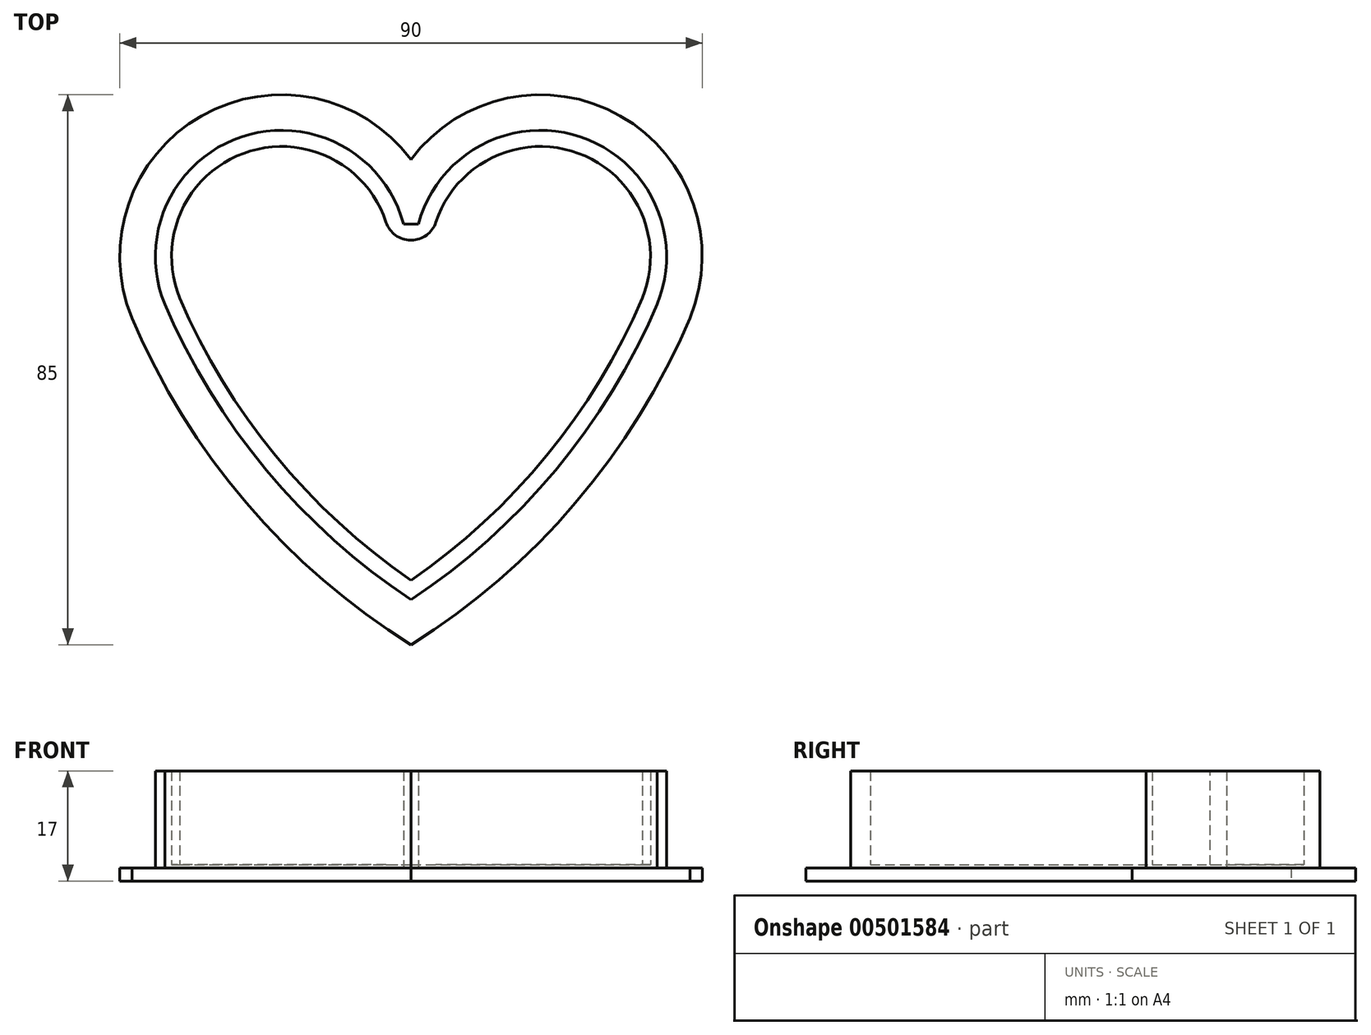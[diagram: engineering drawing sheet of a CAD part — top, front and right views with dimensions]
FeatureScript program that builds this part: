
annotation { "Feature Type Name" : "Feature", "Feature Type Description" : "" }
export const myFeature = defineFeature(function(context is Context, id is Id, definition is map)
    precondition{}
    {
        {
            var Q0;
            Q0=qCreatedBy(makeId("Top.planeOp"),FACE);
            var sketch = newSketch(context, id + "F0", { "sketchPlane" : qUnion([Q0])});
            skArc(sketch, "E0", {"start": v(-43.12, 5.48) * mm, "mid": v(-25.44, -23.07) * mm, "end": v(0, -45) * mm});
            skArc(sketch, "E1", {"start": v(0, 30) * mm, "mid": v(-32.36, 36.73) * mm, "end": v(-43.12, 5.48) * mm});
            skArc(sketch, "E2.MirrorCS", {"start": v(0, 30) * mm, "mid": v(32.36, 36.73) * mm, "end": v(43.12, 5.48) * mm});
            skArc(sketch, "E3.MirrorCS", {"start": v(43.12, 5.48) * mm, "mid": v(25.44, -23.07) * mm, "end": v(0, -45) * mm});
            skPoint(sketch, "E4.orphan", {"position": v(-1.9, 32.24) * mm});
            skPoint(sketch, "E5.orphan", {"position": v(1.9, 32.24) * mm});
            skSolve(sketch);
        }
        {
            var Q0;
            Q0 = qSketchRegion(id + "F0", true);
            extrude(context, id + "F1", {"entities" : qUnion([Q0]), "depth" : 2 * mm});
        }
        {
            var Q0;
            Q0=makeQuery(id+"F1.opExtrude","CAP_FACE",FACE,{"disambiguationData":[OSD([sQuery(id+"F0.wireOp",EDGE,"E0"),sQuery(id+"F0.wireOp",EDGE,"E1"),sQuery(id+"F0.wireOp",EDGE,"E2.MirrorCS"),sQuery(id+"F0.wireOp",EDGE,"E3.MirrorCS")])],"isStart":false});
            var sketch = newSketch(context, id + "F2", { "sketchPlane" : qUnion([Q0])});
            skArc(sketch, "E6.0", {"start": v(-38.06, 7.65) * mm, "mid": v(-22.37, -17.98) * mm, "end": v(0, -38.05) * mm});
            skArc(sketch, "E7.0", {"start": v(-1.16, 20.03) * mm, "mid": v(-26.23, 33.48) * mm, "end": v(-38.04, 7.59) * mm});
            skArc(sketch, "E8.0", {"start": v(1.16, 20.03) * mm, "mid": v(26.23, 33.48) * mm, "end": v(38.04, 7.59) * mm});
            skArc(sketch, "E9.0", {"start": v(38.06, 7.65) * mm, "mid": v(22.37, -17.98) * mm, "end": v(0, -38.05) * mm});
            skLineSegment(sketch, "E10", {"start": v(-1.16, 20.03) * mm, "end": v(1.16, 20.03) * mm});
            skSolve(sketch);
        }
        {
            var Q0;
            Q0 = qSketchRegion(id + "F2", true);
            extrude(context, id + "F3", {"entities" : qUnion([Q0]), "operationType" : NewBodyOperationType.ADD, "depth" : 15 * mm});
        }
        {
            var Q0;
            Q0=makeQuery(id+"F3.opExtrude","CAP_FACE",FACE,{"disambiguationData":[OSD([sQuery(id+"F2.wireOp",EDGE,"E6.0"),sQuery(id+"F2.wireOp",EDGE,"E7.0"),sQuery(id+"F2.wireOp",EDGE,"E8.0"),sQuery(id+"F2.wireOp",EDGE,"E9.0"),sQuery(id+"F2.wireOp",EDGE,"E10")])],"isStart":false});
            shell(context, id + "F4", {"entities" : qUnion([Q0]), "thickness" : 2.5 * mm});
        }
        {
            var Q0;
            Q0=makeQuery(id+"F4.opShell","OFFSET_EDGE",EDGE,{"disambiguationData":[OSD([sQuery(id+"F2.wireOp",EDGE,"E7.0"),sQuery(id+"F2.wireOp",EDGE,"E10")])]});
            var Q1;
            Q1=makeQuery(id+"F4.opShell","OFFSET_EDGE",EDGE,{"disambiguationData":[OSD([sQuery(id+"F2.wireOp",EDGE,"E8.0"),sQuery(id+"F2.wireOp",EDGE,"E10")])]});
            fillet(context, id + "F5", {"entities" : qUnion([Q0, Q1]), "radius" : 4 * mm, "tangentPropagation" : true, "allowEdgeOverflow" : false});
        }
    });
